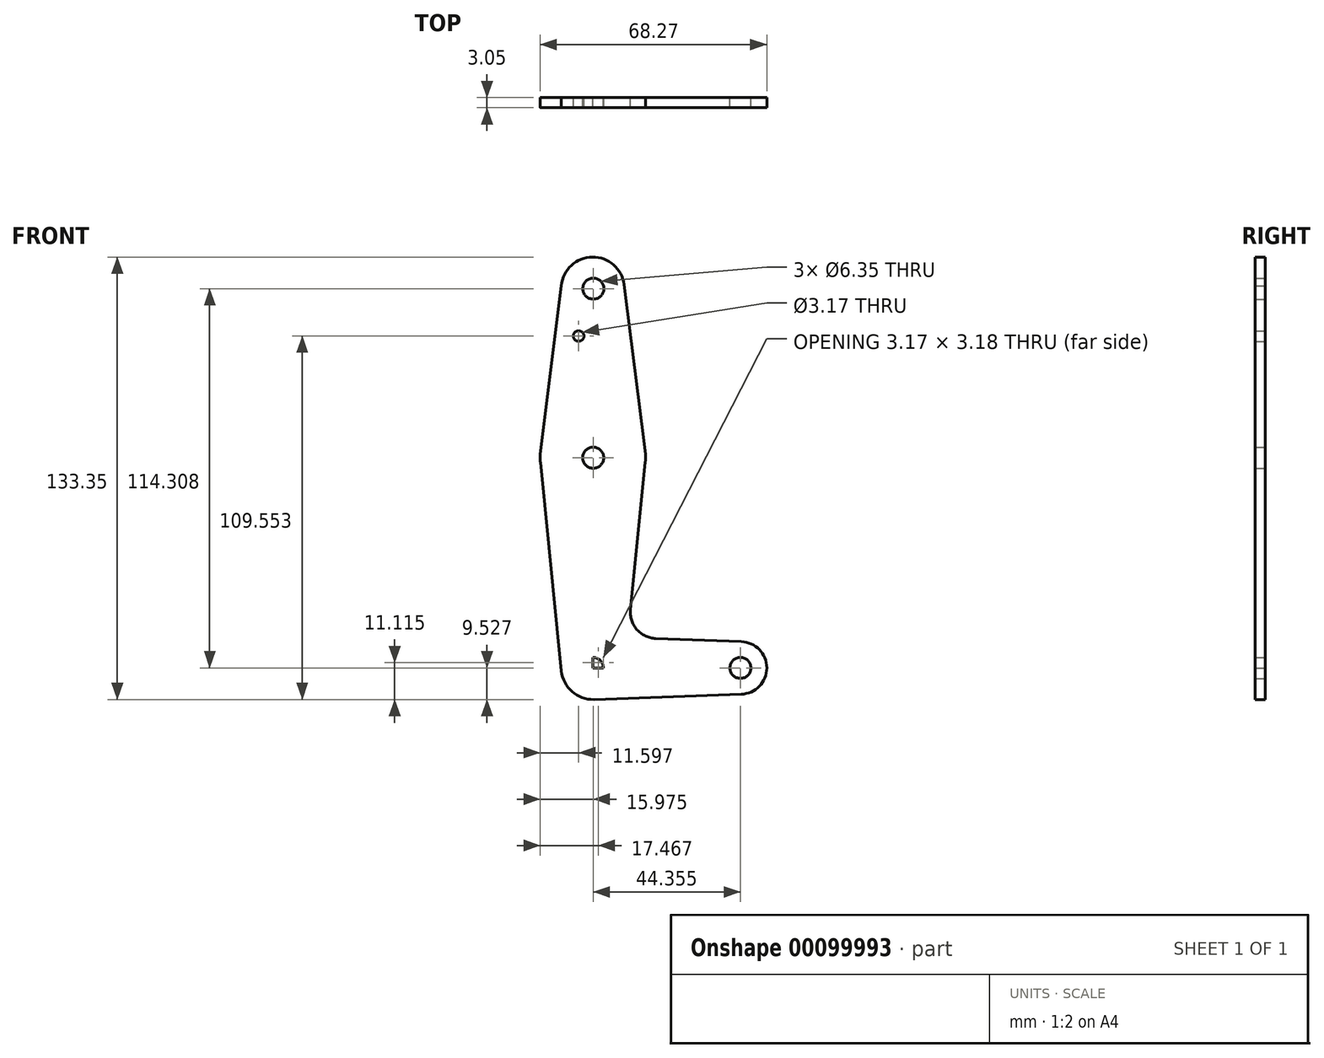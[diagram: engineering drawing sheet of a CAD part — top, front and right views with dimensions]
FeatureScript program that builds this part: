
annotation { "Feature Type Name" : "Feature", "Feature Type Description" : "" }
export const myFeature = defineFeature(function(context is Context, id is Id, definition is map)
    precondition{}
    {
        {
            var Q0;
            Q0=qCreatedBy(makeId("Front.planeOp"),FACE);
            var sketch = newSketch(context, id + "F0", { "sketchPlane" : qUnion([Q0])});
            skLineSegment(sketch, "E0", {"start": v(-26.75, 64.7) * mm, "end": v(-26.75, 13.9) * mm});
            skLineSegment(sketch, "E1", {"start": v(-26.75, 13.9) * mm, "end": v(-26.75, -49.6) * mm});
            skLineSegment(sketch, "E2", {"start": v(-26.75, -49.6) * mm, "end": v(17.7, -49.6) * mm});
            skCircle(sketch, "E3", {"center": v(-26.75, 64.7) * mm, "radius": 9.53 * mm});
            skCircle(sketch, "E4", {"center": v(-26.75, 13.9) * mm, "radius": 15.88 * mm});
            skCircle(sketch, "E5", {"center": v(-26.75, -49.6) * mm, "radius": 9.53 * mm});
            skCircle(sketch, "E6", {"center": v(17.7, -49.6) * mm, "radius": 7.94 * mm});
            skLineSegment(sketch, "E7", {"start": v(-36.23, 65.6) * mm, "end": v(-42.5, 15.9) * mm});
            skLineSegment(sketch, "E8", {"start": v(-17.3, 65.9) * mm, "end": v(-11, 15.9) * mm});
            skLineSegment(sketch, "E9", {"start": v(-42.55, 12.32) * mm, "end": v(-36.23, -50.55) * mm});
            skLineSegment(sketch, "E10", {"start": v(-10.96, 12.32) * mm, "end": v(-15.4, -32) * mm});
            skLineSegment(sketch, "E11", {"start": v(-7.78, -40.74) * mm, "end": v(17.98, -41.66) * mm});
            skLineSegment(sketch, "E12", {"start": v(-26.41, -59.11) * mm, "end": v(17.98, -57.52) * mm});
            skCircle(sketch, "E13", {"center": v(-26.66, 13.76) * mm, "radius": 3.18 * mm});
            skCircle(sketch, "E14", {"center": v(-31.03, 50.43) * mm, "radius": 1.59 * mm});
            skCircle(sketch, "E15", {"center": v(-26.6, 64.72) * mm, "radius": 3.18 * mm});
            skCircle(sketch, "E16", {"center": v(-26.75, -49.6) * mm, "radius": 3.18 * mm});
            skCircle(sketch, "E17", {"center": v(17.7, -49.6) * mm, "radius": 3.18 * mm});
            skPoint(sketch, "E18.newPointA", {"position": v(-17.27, -50.55) * mm});
            skArc(sketch, "E18.filletArc", {"start": v(-15.4, -32) * mm, "mid": v(-13.49, -38.02) * mm, "end": v(-7.78, -40.74) * mm});
            skSolve(sketch);
        }
        {
            var Q0;
            Q0 = qSketchRegion(id + "F0", true);
            var Q1;
            {var subQ0=sQuery(id+"F0.wireOp",EDGE,"E5");var subQ1=sQuery(id+"F0.wireOp",EDGE,"E1");var subQ2=makeQuery(id+"F0.imprint","INTERSECT",VERTEX,{"derivedFrom":[subQ1,subQ0]});Q1=makeQuery(id+"F0.imprint","IMPRINT",FACE,{"disambiguationData":[TD([[makeQuery(id+"F0.imprint","IMPRINT",EDGE,{"disambiguationData":[TD([[subQ2,-1.0]])],"derivedFrom":subQ1}),1.0]])]});}
            var Q2;
            {var subQ0=sQuery(id+"F0.wireOp",EDGE,"E2");var subQ1=sQuery(id+"F0.wireOp",EDGE,"E1");var subQ2=makeQuery(id+"F0.imprint","INTERSECT",VERTEX,{"derivedFrom":[subQ1,subQ0]});Q2=makeQuery(id+"F0.imprint","IMPRINT",FACE,{"disambiguationData":[TD([[makeQuery(id+"F0.imprint","IMPRINT",EDGE,{"disambiguationData":[TD([[subQ2,1.0]])],"derivedFrom":subQ1}),-1.0]])]});}
            extrude(context, id + "F1", {"entities" : qUnion([Q0, Q1, Q2]), "depth" : 3.05 * mm});
        }
    });
